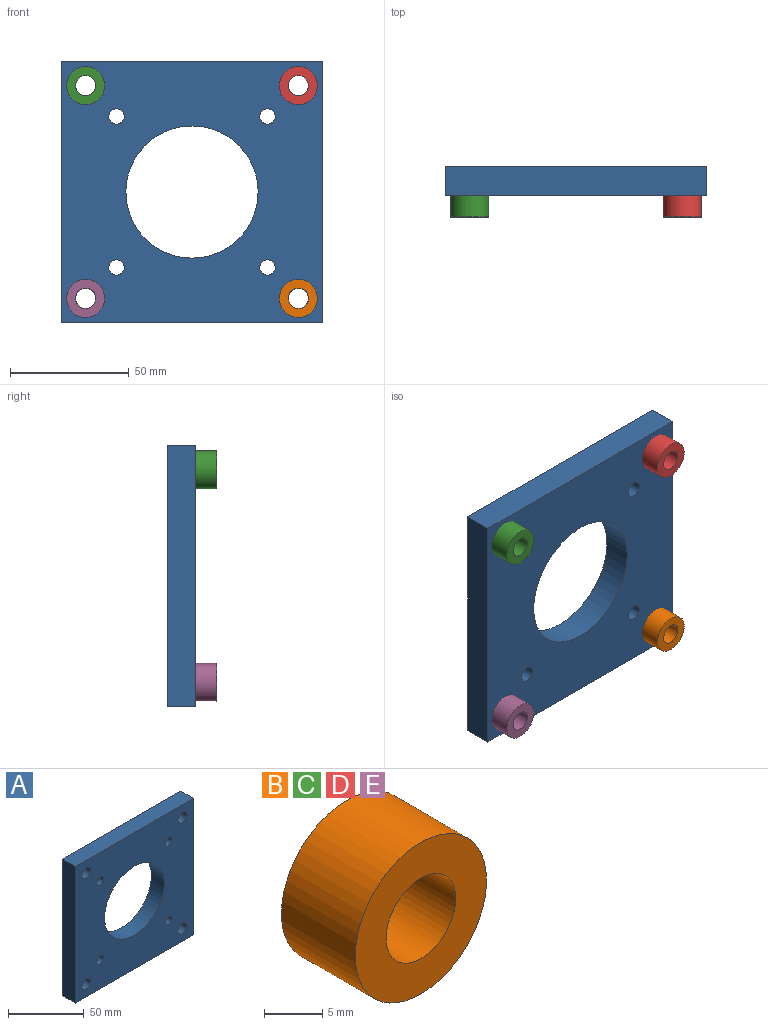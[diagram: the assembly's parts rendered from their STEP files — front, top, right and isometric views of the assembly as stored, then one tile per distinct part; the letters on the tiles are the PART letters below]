
ASSEMBLY  parts=5 mates=1
PART A: 15 faces, bbox 110x12x110 mm
  f0: plane 110x12mm, normal (-1,0,0), area 1320mm2, adj f1,f11,f13,f14
  f1: plane 110x12mm, normal (0,0,-1), area 1320mm2, adj f0,f2,f13,f14
  f2: plane 110x12mm, normal (1,0,0), area 1320mm2, adj f1,f11,f13,f14
  f3: cylinder r=4.25mm len=12mm, axis (0,1,0), area 320.4mm2, adj f13,f14
  f4: cylinder r=4.25mm len=12mm, axis (0,1,0), area 320.4mm2, adj f13,f14
  f5: cylinder r=4.25mm len=12mm, axis (0,1,0), area 320.4mm2, adj f13,f14
  f6: cylinder r=27.8mm len=55.6mm, axis (0,1,0), area 2096.1mm2, adj f13,f14
  f7: cylinder r=3.25mm len=12mm, axis (0,1,0), area 245mm2, adj f13,f14
  f8: cylinder r=3.25mm len=12mm, axis (0,1,0), area 245mm2, adj f13,f14
  f9: cylinder r=3.25mm len=12mm, axis (0,1,0), area 245mm2, adj f13,f14
  f10: cylinder r=3.25mm len=12mm, axis (0,1,0), area 245mm2, adj f13,f14
  f11: plane 110x12mm, normal (0,0,1), area 1320mm2, adj f0,f2,f13,f14
  f12: cylinder r=4.25mm len=12mm, axis (0,1,0), area 320.4mm2, adj f13,f14
  f13: plane 110x110mm, normal (0,-1,0), area 9312.3mm2, adj f0,f1,f2,f3,f4,f5,f6,f7
  f14: plane 110x110mm, normal (0,1,0), area 9312.3mm2, adj f0,f1,f2,f3,f4,f5,f6,f7
PART B: 4 faces, bbox 16x9x16 mm
  f0: cylinder r=4.25mm len=9mm, axis (0,1,0), area 240.3mm2, adj f2,f3
  f1: cylinder r=8mm len=16mm, axis (0,1,0), area 452.4mm2, adj f2,f3
  f2: plane 16x16mm, normal (0,-1,0), area 144.3mm2, adj f0,f1
  f3: plane 16x16mm, normal (0,1,0), area 144.3mm2, adj f0,f1
PART C: same geometry as B
PART D: same geometry as B
PART E: same geometry as B
PLACE A t=(-39.71,5.82,-40.52)mm fixed
PLACE B rot(axis=(1,0,0),180deg) t=(45.04,-15.18,-45.27)mm
PLACE C rot(axis=(1,0,0),180deg) t=(-44.46,-15.18,44.23)mm
PLACE D rot(axis=(1,0,0),180deg) t=(45.04,-15.18,44.23)mm
PLACE E rot(axis=(1,0,0),180deg) t=(-44.46,-15.18,-45.27)mm
MATE fastened A.f5 <-> C.f0  axis (0,-1,0) through (-44.46,-6.18,44.23)mm
